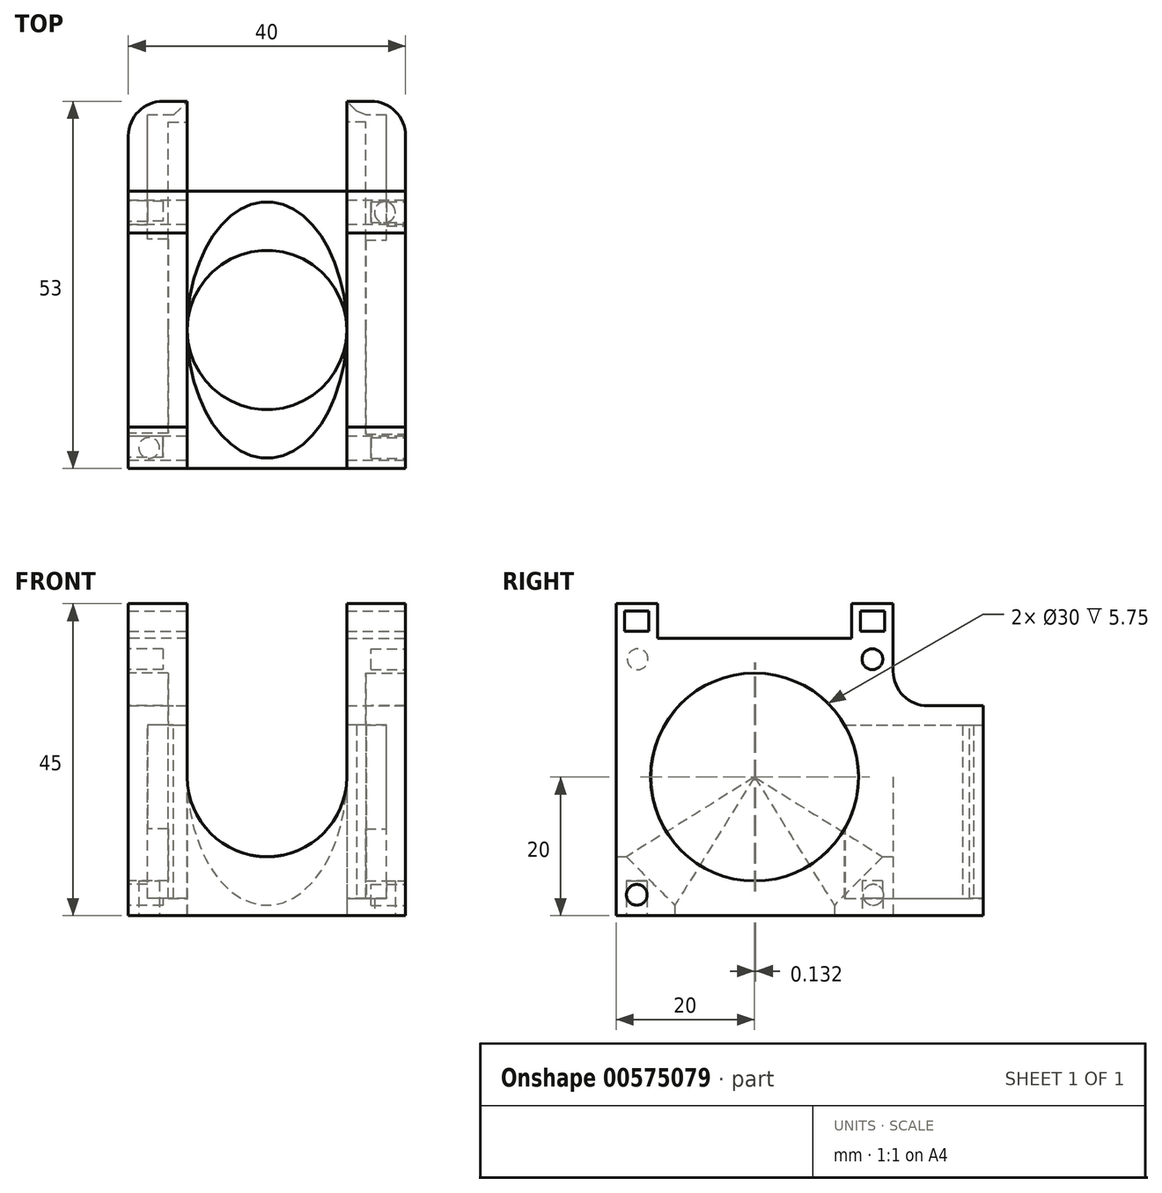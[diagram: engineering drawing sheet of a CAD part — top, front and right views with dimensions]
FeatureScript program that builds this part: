
annotation { "Feature Type Name" : "Feature", "Feature Type Description" : "" }
export const myFeature = defineFeature(function(context is Context, id is Id, definition is map)
    precondition{}
    {
        {
            var Q0;
            Q0=qCreatedBy(makeId("Front.planeOp"),FACE);
            var sketch = newSketch(context, id + "F0", { "sketchPlane" : qUnion([Q0])});
            skLineSegment(sketch, "E0", {"start": v(-20, 20) * mm, "end": v(-20, -20) * mm});
            skLineSegment(sketch, "E1", {"start": v(-20, -20) * mm, "end": v(20, -20) * mm});
            skLineSegment(sketch, "E2", {"start": v(20, -20) * mm, "end": v(20, 20) * mm});
            skLineSegment(sketch, "E3", {"start": v(20, 20) * mm, "end": v(11.5, 20) * mm});
            skLineSegment(sketch, "E4", {"start": v(11.5, 20) * mm, "end": v(11.5, 0) * mm});
            skLineSegment(sketch, "E5", {"start": v(-11.5, 0) * mm, "end": v(-11.5, 20) * mm});
            skLineSegment(sketch, "E6", {"start": v(-20, 20) * mm, "end": v(-11.5, 20) * mm});
            skLineSegment(sketch, "E7", {"start": v(0, 35.37) * mm, "end": v(0, -31.05) * mm, "construction": true});
            skLineSegment(sketch, "E8", {"start": v(-42.53, 0) * mm, "end": v(36.7, 0) * mm, "construction": true});
            skArc(sketch, "E9", {"start": v(-11.5, 0) * mm, "mid": v(0, -11.5) * mm, "end": v(11.5, 0) * mm});
            skSolve(sketch);
        }
        {
            var Q0;
            Q0 = qSketchRegion(id + "F0", true);
            extrude(context, id + "F1", {"entities" : qUnion([Q0]), "depth" : 40 * mm, "offsetDistance" : 25 * mm});
        }
        {
            var Q0;
            Q0=makeQuery(id+"F1.opExtrude","SWEPT_FACE",FACE,{"disambiguationData":[OSD([sQuery(id+"F0.wireOp",EDGE,"E1")])]});
            var sketch = newSketch(context, id + "F2", { "sketchPlane" : qUnion([Q0])});
            skLineSegment(sketch, "E10", {"start": v(-20, 40) * mm, "end": v(20, 0) * mm, "construction": true});
            skLineSegment(sketch, "E11", {"start": v(-20, 0) * mm, "end": v(20, 40) * mm, "construction": true});
            skCircle(sketch, "E12", {"center": v(0, 20) * mm, "radius": 11.5 * mm});
            skLineSegment(sketch, "E13", {"start": v(-17, 47.17) * mm, "end": v(-17, -3.7) * mm, "construction": true});
            skLineSegment(sketch, "E14", {"start": v(17, 46.33) * mm, "end": v(17, -4.22) * mm, "construction": true});
            skCircle(sketch, "E15", {"center": v(-17, 37) * mm, "radius": 1.5 * mm});
            skCircle(sketch, "E16", {"center": v(17, 3) * mm, "radius": 1.5 * mm});
            skSolve(sketch);
        }
        {
            var Q0;
            Q0=makeQuery(id+"F2.imprint","IMPRINT",FACE,{"disambiguationData":[TD([[makeQuery(id+"F2.imprint","IMPRINT",EDGE,{"derivedFrom":sQuery(id+"F2.wireOp",EDGE,"E12")}),1.0]])]});
            extrude(context, id + "F3", {"entities" : qUnion([Q0]), "operationType" : NewBodyOperationType.REMOVE, "oppositeDirection" : true, "depth" : 25 * mm, "offsetDistance" : 25 * mm});
        }
        {
            var Q0;
            Q0=makeQuery(id+"F2.imprint","IMPRINT",FACE,{"disambiguationData":[TD([[makeQuery(id+"F2.imprint","IMPRINT",EDGE,{"derivedFrom":sQuery(id+"F2.wireOp",EDGE,"E16")}),1.0]])]});
            var Q1;
            Q1=makeQuery(id+"F2.imprint","IMPRINT",FACE,{"disambiguationData":[TD([[makeQuery(id+"F2.imprint","IMPRINT",EDGE,{"derivedFrom":sQuery(id+"F2.wireOp",EDGE,"E15")}),1.0]])]});
            extrude(context, id + "F4", {"entities" : qUnion([Q0, Q1]), "operationType" : NewBodyOperationType.REMOVE, "oppositeDirection" : true, "depth" : 5 * mm, "offsetDistance" : 25 * mm});
        }
        {
            var Q0;
            Q0=makeQuery(id+"F1.opExtrude","SWEPT_FACE",FACE,{"disambiguationData":[OSD([sQuery(id+"F0.wireOp",EDGE,"E2")])]});
            var sketch = newSketch(context, id + "F5", { "sketchPlane" : qUnion([Q0])});
            skLineSegment(sketch, "E17", {"start": v(-40, -20) * mm, "end": v(0, 20) * mm, "construction": true});
            skCircle(sketch, "E18", {"center": v(-20, 0) * mm, "radius": 15 * mm});
            skLineSegment(sketch, "E19", {"start": v(7.6, -17) * mm, "end": v(-44.55, -17) * mm, "construction": true});
            skLineSegment(sketch, "E20", {"start": v(-46.22, 17) * mm, "end": v(4.75, 17) * mm, "construction": true});
            skCircle(sketch, "E21", {"center": v(-37, -17) * mm, "radius": 1.5 * mm});
            skCircle(sketch, "E22", {"center": v(-3, 17) * mm, "radius": 1.5 * mm});
            skSolve(sketch);
        }
        {
            var Q0;
            Q0=makeQuery(id+"F5.imprint","IMPRINT",FACE,{"disambiguationData":[TD([[makeQuery(id+"F5.imprint","IMPRINT",EDGE,{"derivedFrom":sQuery(id+"F5.wireOp",EDGE,"E18")}),1.0]])]});
            extrude(context, id + "F6", {"entities" : qUnion([Q0]), "operationType" : NewBodyOperationType.REMOVE, "oppositeDirection" : true, "depth" : 3 * mm, "offsetDistance" : 25 * mm});
        }
        {
            var Q0;
            Q0=makeQuery(id+"F5.imprint","IMPRINT",FACE,{"disambiguationData":[TD([[makeQuery(id+"F5.imprint","IMPRINT",EDGE,{"derivedFrom":sQuery(id+"F5.wireOp",EDGE,"E21")}),1.0]])]});
            var Q1;
            Q1=makeQuery(id+"F5.imprint","IMPRINT",FACE,{"disambiguationData":[TD([[makeQuery(id+"F5.imprint","IMPRINT",EDGE,{"derivedFrom":sQuery(id+"F5.wireOp",EDGE,"E22")}),1.0]])]});
            var Q2;
            Q2=sQuery(id+"F5.wireOp",EDGE,"E21");
            var Q3;
            Q3=sQuery(id+"F5.wireOp",EDGE,"E22");
            extrude(context, id + "F7", {"entities" : qUnion([Q0, Q1]), "operationType" : NewBodyOperationType.REMOVE, "surfaceEntities" : qUnion([Q2, Q3]), "oppositeDirection" : true, "depth" : 5 * mm, "offsetDistance" : 25 * mm});
        }
        {
            var Q0;
            Q0=makeQuery(id+"F1.opExtrude","CAP_FACE",FACE,{"disambiguationData":[OSD([sQuery(id+"F0.wireOp",EDGE,"E0"),sQuery(id+"F0.wireOp",EDGE,"E1"),sQuery(id+"F0.wireOp",EDGE,"E2"),sQuery(id+"F0.wireOp",EDGE,"E3"),sQuery(id+"F0.wireOp",EDGE,"E4"),sQuery(id+"F0.wireOp",EDGE,"E5"),sQuery(id+"F0.wireOp",EDGE,"E6"),sQuery(id+"F0.wireOp",EDGE,"E9")])],"isStart":true});
            var sketch = newSketch(context, id + "F8", { "sketchPlane" : qUnion([Q0])});
            skLineSegment(sketch, "E23", {"start": v(-20, -20) * mm, "end": v(-11.5, 20) * mm, "construction": true});
            skLineSegment(sketch, "E24.bottom", {"start": v(-14.25, 7.5) * mm, "end": v(-17.25, 7.5) * mm});
            skLineSegment(sketch, "E24.top", {"start": v(-14.25, -7.5) * mm, "end": v(-17.25, -7.5) * mm});
            skLineSegment(sketch, "E24.left", {"start": v(-14.25, 7.5) * mm, "end": v(-14.25, -7.5) * mm});
            skLineSegment(sketch, "E24.right", {"start": v(-17.25, 7.5) * mm, "end": v(-17.25, -7.5) * mm});
            skPoint(sketch, "E24.middle", {"position": v(-15.75, 0) * mm});
            skLineSegment(sketch, "E25", {"start": v(11.5, 20) * mm, "end": v(20, -20) * mm, "construction": true});
            skLineSegment(sketch, "E26.bottom", {"start": v(14.25, -7.5) * mm, "end": v(17.25, -7.5) * mm});
            skLineSegment(sketch, "E26.top", {"start": v(14.25, 7.5) * mm, "end": v(17.25, 7.5) * mm});
            skLineSegment(sketch, "E26.left", {"start": v(14.25, -7.5) * mm, "end": v(14.25, 7.5) * mm});
            skLineSegment(sketch, "E26.right", {"start": v(17.25, -7.5) * mm, "end": v(17.25, 7.5) * mm});
            skPoint(sketch, "E26.middle", {"position": v(15.75, 0) * mm});
            skSolve(sketch);
        }
        {
            var Q0;
            Q0 = qSketchRegion(id + "F8", true);
            extrude(context, id + "F9", {"entities" : qUnion([Q0]), "operationType" : NewBodyOperationType.REMOVE, "oppositeDirection" : true, "depth" : 20 * mm, "offsetDistance" : 25 * mm});
        }
        {
            var Q0;
            Q0=makeQuery(id+"F1.opExtrude","SWEPT_FACE",FACE,{"disambiguationData":[OSD([sQuery(id+"F0.wireOp",EDGE,"E0")])]});
            var sketch = newSketch(context, id + "F10", { "sketchPlane" : qUnion([Q0])});
            skLineSegment(sketch, "E27", {"start": v(-0.13, -20) * mm, "end": v(39.87, 20) * mm, "construction": true});
            skCircle(sketch, "E28", {"center": v(19.87, 0) * mm, "radius": 15 * mm});
            skLineSegment(sketch, "E29", {"start": v(47.47, -17) * mm, "end": v(-4.68, -17) * mm, "construction": true});
            skLineSegment(sketch, "E30", {"start": v(-6.36, 17) * mm, "end": v(44.62, 17) * mm, "construction": true});
            skCircle(sketch, "E31", {"center": v(2.87, -17) * mm, "radius": 1.5 * mm});
            skCircle(sketch, "E32", {"center": v(36.87, 17) * mm, "radius": 1.5 * mm});
            skSolve(sketch);
        }
        {
            var Q0;
            Q0=makeQuery(id+"F10.imprint","IMPRINT",FACE,{"disambiguationData":[TD([[makeQuery(id+"F10.imprint","IMPRINT",EDGE,{"derivedFrom":sQuery(id+"F10.wireOp",EDGE,"E28")}),1.0]])]});
            extrude(context, id + "F11", {"entities" : qUnion([Q0]), "operationType" : NewBodyOperationType.REMOVE, "oppositeDirection" : true, "depth" : 3 * mm, "offsetDistance" : 25 * mm});
        }
        {
            var Q0;
            Q0=makeQuery(id+"F10.imprint","IMPRINT",FACE,{"disambiguationData":[TD([[makeQuery(id+"F10.imprint","IMPRINT",EDGE,{"derivedFrom":sQuery(id+"F10.wireOp",EDGE,"E32")}),1.0]])]});
            var Q1;
            Q1=makeQuery(id+"F10.imprint","IMPRINT",FACE,{"disambiguationData":[TD([[makeQuery(id+"F10.imprint","IMPRINT",EDGE,{"derivedFrom":sQuery(id+"F10.wireOp",EDGE,"E31")}),1.0]])]});
            extrude(context, id + "F12", {"entities" : qUnion([Q0, Q1]), "operationType" : NewBodyOperationType.REMOVE, "oppositeDirection" : true, "depth" : 5 * mm, "offsetDistance" : 25 * mm});
        }
        {
            var Q0;
            Q0=makeQuery(id+"F1.opExtrude","CAP_FACE",FACE,{"disambiguationData":[OSD([sQuery(id+"F0.wireOp",EDGE,"E0"),sQuery(id+"F0.wireOp",EDGE,"E1"),sQuery(id+"F0.wireOp",EDGE,"E2"),sQuery(id+"F0.wireOp",EDGE,"E3"),sQuery(id+"F0.wireOp",EDGE,"E4"),sQuery(id+"F0.wireOp",EDGE,"E5"),sQuery(id+"F0.wireOp",EDGE,"E6"),sQuery(id+"F0.wireOp",EDGE,"E9")])],"isStart":true});
            extrude(context, id + "F13", {"entities" : qUnion([Q0]), "operationType" : NewBodyOperationType.ADD, "depth" : 13 * mm, "offsetDistance" : 25 * mm});
        }
        {
            var Q0;
            Q0=makeQuery(id+"F13.opExtrude","CAP_FACE",FACE,{"disambiguationData":[OSD([sQuery(id+"F0.wireOp",EDGE,"E0"),sQuery(id+"F0.wireOp",EDGE,"E1"),sQuery(id+"F0.wireOp",EDGE,"E2"),sQuery(id+"F0.wireOp",EDGE,"E3"),sQuery(id+"F0.wireOp",EDGE,"E4"),sQuery(id+"F0.wireOp",EDGE,"E5"),sQuery(id+"F0.wireOp",EDGE,"E6"),sQuery(id+"F0.wireOp",EDGE,"E9")])],"isStart":false});
            var sketch = newSketch(context, id + "F14", { "sketchPlane" : qUnion([Q0])});
            skLineSegment(sketch, "E33", {"start": v(20, -10.5) * mm, "end": v(-20, -10.5) * mm});
            skLineSegment(sketch, "E34", {"start": v(11.5, 20) * mm, "end": v(11.5, -10.5) * mm});
            skLineSegment(sketch, "E35", {"start": v(-11.5, 20) * mm, "end": v(-11.5, -10.5) * mm});
            skLineSegment(sketch, "E36", {"start": v(20, 10.28) * mm, "end": v(-20, 10.28) * mm});
            skSolve(sketch);
        }
        {
            var Q0;
            {var subQ0=makeQuery(id+"F13.opExtrude","CAP_EDGE",EDGE,{"disambiguationData":[OSD([sQuery(id+"F0.wireOp",EDGE,"E1")])],"isStart":false});Q0=makeQuery(id+"F14.imprint","IMPRINT",FACE,{"disambiguationData":[TD([[makeQuery(id+"F14.imprint","IMPRINT",EDGE,{"derivedFrom":subQ0}),-1.0]])]});}
            var Q1;
            {var subQ0=sQuery(id+"F14.wireOp",EDGE,"E34");var subQ1=sQuery(id+"F14.wireOp",EDGE,"E33");var subQ2=makeQuery(id+"F14.imprint","INTERSECT",VERTEX,{"derivedFrom":[subQ1,subQ0]});Q1=makeQuery(id+"F14.imprint","IMPRINT",FACE,{"disambiguationData":[TD([[makeQuery(id+"F14.imprint","IMPRINT",EDGE,{"disambiguationData":[TD([[subQ2,-1.0]])],"derivedFrom":subQ1}),-1.0]])]});}
            var Q2;
            {var subQ0=sQuery(id+"F14.wireOp",EDGE,"E35");var subQ1=sQuery(id+"F14.wireOp",EDGE,"E33");var subQ2=makeQuery(id+"F14.imprint","INTERSECT",VERTEX,{"derivedFrom":[subQ1,subQ0]});Q2=makeQuery(id+"F14.imprint","IMPRINT",FACE,{"disambiguationData":[TD([[makeQuery(id+"F14.imprint","IMPRINT",EDGE,{"disambiguationData":[TD([[subQ2,1.0]])],"derivedFrom":subQ1}),-1.0]])]});}
            var Q3;
            {var subQ1=makeQuery(id+"F13.opExtrude","CAP_EDGE",EDGE,{"disambiguationData":[OSD([sQuery(id+"F0.wireOp",EDGE,"E6")])],"isStart":false});Q3=makeQuery(id+"F14.imprint","IMPRINT",FACE,{"disambiguationData":[TD([[makeQuery(id+"F14.imprint","IMPRINT",EDGE,{"derivedFrom":subQ1}),1.0]])]});}
            var Q4;
            {var subQ1=makeQuery(id+"F13.opExtrude","CAP_EDGE",EDGE,{"disambiguationData":[OSD([sQuery(id+"F0.wireOp",EDGE,"E3")])],"isStart":false});Q4=makeQuery(id+"F14.imprint","IMPRINT",FACE,{"disambiguationData":[TD([[makeQuery(id+"F14.imprint","IMPRINT",EDGE,{"derivedFrom":subQ1}),-1.0]])]});}
            extrude(context, id + "F15", {"entities" : qUnion([Q0, Q1, Q2, Q3, Q4]), "operationType" : NewBodyOperationType.REMOVE, "oppositeDirection" : true, "depth" : 13 * mm, "offsetDistance" : 25 * mm});
        }
        {
            var Q0;
            Q0=makeQuery(id+"F14.imprint","IMPRINT",FACE,{"disambiguationData":[TD([[makeQuery(id+"F14.imprint","IMPRINT",EDGE,{"derivedFrom":makeQuery(id+"F13.opExtrude","CAP_EDGE",EDGE,{"disambiguationData":[OSD([sQuery(id+"F8.wireOp",EDGE,"E26.bottom")])],"isStart":false})}),-1.0]])]});
            var sketch = newSketch(context, id + "F16", { "sketchPlane" : qUnion([Q0])});
            skLineSegment(sketch, "E37.0", {"start": v(11.5, 20) * mm, "end": v(11.5, -10.5) * mm});
            skLineSegment(sketch, "E38.0", {"start": v(14.25, -7.5) * mm, "end": v(14.25, 7.5) * mm});
            skLineSegment(sketch, "E39.bottom", {"start": v(14.25, -7.5) * mm, "end": v(11.5, -7.5) * mm});
            skLineSegment(sketch, "E39.top", {"start": v(14.25, 7.5) * mm, "end": v(11.5, 7.5) * mm});
            skLineSegment(sketch, "E39.right", {"start": v(11.5, -7.5) * mm, "end": v(11.5, 7.5) * mm});
            skLineSegment(sketch, "E40.0", {"start": v(-14.25, 7.5) * mm, "end": v(-14.25, -7.5) * mm});
            skLineSegment(sketch, "E41.0", {"start": v(-11.5, 20) * mm, "end": v(-11.5, -10.5) * mm});
            skLineSegment(sketch, "E42.bottom", {"start": v(-14.25, -7.5) * mm, "end": v(-11.5, -7.5) * mm});
            skLineSegment(sketch, "E42.top", {"start": v(-14.25, 7.5) * mm, "end": v(-11.5, 7.5) * mm});
            skLineSegment(sketch, "E42.left", {"start": v(-14.25, -7.5) * mm, "end": v(-14.25, 7.5) * mm});
            skLineSegment(sketch, "E42.right", {"start": v(-11.5, -7.5) * mm, "end": v(-11.5, 7.5) * mm});
            skSolve(sketch);
        }
        {
            var Q0;
            Q0 = qSketchRegion(id + "F16", true);
            extrude(context, id + "F17", {"entities" : qUnion([Q0]), "operationType" : NewBodyOperationType.REMOVE, "oppositeDirection" : true, "depth" : 3 * mm, "offsetDistance" : 25 * mm});
        }
        {
            var Q0;
            {var subQ0=sQuery(id+"F14.wireOp",EDGE,"E36");Q0=makeQuery(id+"F15.boolean.opBoolean","COPY",FACE,{"derivedFrom":makeQuery(id+"F15.opExtrude","SWEPT_FACE",FACE,{"disambiguationData":[OSD([subQ0]),TDD([makeQuery(id+"F14.imprint","IMPRINT",EDGE,{"disambiguationData":[TD([[makeQuery(id+"F14.imprint","INTERSECT",VERTEX,{"derivedFrom":[makeQuery(id+"F13.opExtrude","CAP_EDGE",EDGE,{"disambiguationData":[OSD([sQuery(id+"F0.wireOp",EDGE,"E0")])],"isStart":false}),subQ0]}),-1.0]])],"derivedFrom":subQ0})])]})});}
            var sketch = newSketch(context, id + "F18", { "sketchPlane" : qUnion([Q0])});
            skLineSegment(sketch, "E43", {"start": v(-20, 11) * mm, "end": v(-11.5, 11) * mm});
            skSolve(sketch);
        }
        {
            var Q0;
            {var subQ0=sQuery(id+"F18.wireOp",EDGE,"E43");Q0=makeQuery(id+"F18.imprint","IMPRINT",FACE,{"disambiguationData":[TD([[makeQuery(id+"F18.imprint","IMPRINT",EDGE,{"derivedFrom":subQ0}),1.0]])]});}
            extrude(context, id + "F19", {"entities" : qUnion([Q0]), "operationType" : NewBodyOperationType.ADD, "oppositeDirection" : true, "depth" : 18 * mm, "offsetDistance" : 25 * mm});
        }
        {
            var Q0;
            {var subQ0=sQuery(id+"F0.wireOp",EDGE,"E4");var subQ1=sQuery(id+"F0.wireOp",EDGE,"E2");var subQ10=sQuery(id+"F0.wireOp",EDGE,"E9");Q0=makeQuery(id+"F15.boolean.opBoolean","SPLIT",FACE,{"disambiguationData":[TD([makeQuery(id+"F1.opExtrude","SWEPT_FACE",FACE,{"disambiguationData":[OSD([subQ1])]})])],"derivedFrom":makeQuery(id+"F13.opExtrude","CAP_FACE",FACE,{"disambiguationData":[OSD([sQuery(id+"F0.wireOp",EDGE,"E0"),sQuery(id+"F0.wireOp",EDGE,"E1"),subQ1,sQuery(id+"F0.wireOp",EDGE,"E3"),subQ0,sQuery(id+"F0.wireOp",EDGE,"E5"),sQuery(id+"F0.wireOp",EDGE,"E6"),subQ10])],"isStart":false})});}
            var sketch = newSketch(context, id + "F20", { "sketchPlane" : qUnion([Q0])});
            skLineSegment(sketch, "E44.bottom", {"start": v(-20, 10.28) * mm, "end": v(-11.5, 10.28) * mm});
            skLineSegment(sketch, "E44.top", {"start": v(-20, -10.5) * mm, "end": v(-11.5, -10.5) * mm});
            skLineSegment(sketch, "E44.left", {"start": v(-20, 10.28) * mm, "end": v(-20, -10.5) * mm});
            skLineSegment(sketch, "E44.right", {"start": v(-11.5, 10.28) * mm, "end": v(-11.5, -10.5) * mm});
            skSolve(sketch);
        }
        {
            var Q0;
            Q0 = qSketchRegion(id + "F20", true);
            extrude(context, id + "F21", {"entities" : qUnion([Q0]), "operationType" : NewBodyOperationType.ADD, "oppositeDirection" : true, "depth" : 2 * mm, "offsetDistance" : 25 * mm});
        }
        {
            var Q0;
            Q0=makeQuery(id+"F19.opExtrude","SWEPT_EDGE",EDGE,{"disambiguationData":[OSD([sQuery(id+"F14.wireOp",EDGE,"E34"),sQuery(id+"F14.wireOp",EDGE,"E36"),sQuery(id+"F18.wireOp",EDGE,"E43")])]});
            var Q1;
            Q1=makeQuery(id+"F17.boolean.opBoolean","COPY",EDGE,{"derivedFrom":makeQuery(id+"F17.opExtrude","CAP_EDGE",EDGE,{"disambiguationData":[OSD([sQuery(id+"F16.wireOp",EDGE,"E38.0")])],"isStart":false})});
            var Q2;
            Q2=makeQuery(id+"F17.boolean.opBoolean","COPY",EDGE,{"derivedFrom":makeQuery(id+"F17.opExtrude","CAP_EDGE",EDGE,{"disambiguationData":[OSD([sQuery(id+"F16.wireOp",EDGE,"E42.left")])],"isStart":false})});
            var Q3;
            Q3=makeQuery(id+"F21.opExtrude","CAP_EDGE",EDGE,{"disambiguationData":[OSD([sQuery(id+"F20.wireOp",EDGE,"E44.right")])],"isStart":false});
            chamfer(context, id + "F22", {"entities" : qUnion([Q0, Q1, Q2, Q3]), "width" : 2 * mm, "tangentPropagation" : true});
        }
        {
            var Q0;
            {var subQ0=sQuery(id+"F18.wireOp",EDGE,"E43");Q0=makeQuery(id+"F22.opChamfer","BLEND_EDGE",EDGE,{"blendedFrom":[makeQuery(id+"F19.opExtrude","SWEPT_EDGE",EDGE,{"disambiguationData":[OSD([sQuery(id+"F14.wireOp",EDGE,"E34"),sQuery(id+"F14.wireOp",EDGE,"E36"),subQ0])]}),makeQuery(id+"FBn1wkCs05xnqRL_1.opFillet","BLEND_FACE",FACE,{"disambiguationData":[OSD([sQuery(id+"F8.wireOp",EDGE,"E26.right"),subQ0])]})],"blendedInto":[makeQuery(id+"FBn1wkCs05xnqRL_1.opFillet","BLEND_FACE",FACE,{"disambiguationData":[OSD([sQuery(id+"F8.wireOp",EDGE,"E26.right"),subQ0])]})]});}
            var Q1;
            {var subQ0=sQuery(id+"F20.wireOp",EDGE,"E44.right");Q1=makeQuery(id+"F22.opChamfer","BLEND_EDGE",EDGE,{"blendedFrom":[makeQuery(id+"F21.opExtrude","CAP_EDGE",EDGE,{"disambiguationData":[OSD([subQ0])],"isStart":false}),makeQuery(id+"F21.opExtrude","CAP_FACE",FACE,{"disambiguationData":[OSD([sQuery(id+"F20.wireOp",EDGE,"E44.bottom"),sQuery(id+"F20.wireOp",EDGE,"E44.top"),sQuery(id+"F20.wireOp",EDGE,"E44.left"),subQ0])],"isStart":false})],"blendedInto":[makeQuery(id+"F21.opExtrude","CAP_FACE",FACE,{"disambiguationData":[OSD([sQuery(id+"F20.wireOp",EDGE,"E44.bottom"),sQuery(id+"F20.wireOp",EDGE,"E44.top"),sQuery(id+"F20.wireOp",EDGE,"E44.left"),subQ0])],"isStart":false})]});}
            chamfer(context, id + "F23", {"entities" : qUnion([Q0, Q1]), "width" : 2 * mm, "tangentPropagation" : true});
        }
        {
            var Q0;
            Q0=makeQuery(id+"F3.boolean.opBoolean","COPY",EDGE,{"derivedFrom":makeQuery(id+"F3.opExtrude","CAP_EDGE",EDGE,{"disambiguationData":[OSD([sQuery(id+"F2.wireOp",EDGE,"E12")])],"isStart":true})});
            var Q1;
            Q1=makeQuery(id+"F3.boolean.opBoolean","INTERSECT",EDGE,{"disambiguationData":[OD(1.0)],"derivedFrom":[makeQuery(id+"F1.opExtrude","SWEPT_FACE",FACE,{"disambiguationData":[OSD([sQuery(id+"F0.wireOp",EDGE,"E9")])]}),makeQuery(id+"F3.opExtrude","SWEPT_FACE",FACE,{"disambiguationData":[OSD([sQuery(id+"F2.wireOp",EDGE,"E12")])]})]});
            var Q2;
            Q2=makeQuery(id+"F3.boolean.opBoolean","INTERSECT",EDGE,{"disambiguationData":[OD(0.0)],"derivedFrom":[makeQuery(id+"F1.opExtrude","SWEPT_FACE",FACE,{"disambiguationData":[OSD([sQuery(id+"F0.wireOp",EDGE,"E9")])]}),makeQuery(id+"F3.opExtrude","SWEPT_FACE",FACE,{"disambiguationData":[OSD([sQuery(id+"F2.wireOp",EDGE,"E12")])]})]});
            chamfer(context, id + "F24", {"entities" : qUnion([Q0, Q1, Q2]), "width" : 7 * mm, "tangentPropagation" : true});
        }
        {
            var Q0;
            Q0=makeQuery(id+"F11.boolean.opBoolean","COPY",FACE,{"derivedFrom":makeQuery(id+"F11.opExtrude","CAP_FACE",FACE,{"disambiguationData":[OSD([sQuery(id+"F10.wireOp",EDGE,"E28")])],"isStart":false})});
            extrude(context, id + "F25", {"entities" : qUnion([Q0]), "operationType" : NewBodyOperationType.REMOVE, "oppositeDirection" : true, "depth" : 2.75 * mm, "offsetDistance" : 25 * mm});
        }
        {
            var Q0;
            Q0=makeQuery(id+"F6.boolean.opBoolean","COPY",FACE,{"derivedFrom":makeQuery(id+"F6.opExtrude","CAP_FACE",FACE,{"disambiguationData":[OSD([sQuery(id+"F5.wireOp",EDGE,"E18")])],"isStart":false})});
            extrude(context, id + "F26", {"entities" : qUnion([Q0]), "operationType" : NewBodyOperationType.REMOVE, "oppositeDirection" : true, "depth" : 2.75 * mm, "offsetDistance" : 25 * mm});
        }
        {
            var Q0;
            {var subQ0=sQuery(id+"F0.wireOp",EDGE,"E3");Q0=makeQuery(id+"F13.boolean.opBoolean","MERGE",FACE,{"derivedFrom":[makeQuery(id+"F1.opExtrude","SWEPT_FACE",FACE,{"disambiguationData":[OSD([subQ0])]}),makeQuery(id+"F13.opExtrude","SWEPT_FACE",FACE,{"disambiguationData":[OSD([subQ0])]})]});}
            var sketch = newSketch(context, id + "F27", { "sketchPlane" : qUnion([Q0])});
            skLineSegment(sketch, "E45.bottom", {"start": v(11.5, -40) * mm, "end": v(20, -40) * mm});
            skLineSegment(sketch, "E45.top", {"start": v(11.5, -34) * mm, "end": v(20, -34) * mm});
            skLineSegment(sketch, "E45.left", {"start": v(11.5, -40) * mm, "end": v(11.5, -34) * mm});
            skLineSegment(sketch, "E45.right", {"start": v(20, -40) * mm, "end": v(20, -34) * mm});
            skLineSegment(sketch, "E46.bottom", {"start": v(11.5, 0) * mm, "end": v(20, 0) * mm});
            skLineSegment(sketch, "E46.top", {"start": v(11.5, -6) * mm, "end": v(20, -6) * mm});
            skLineSegment(sketch, "E46.left", {"start": v(11.5, 0) * mm, "end": v(11.5, -6) * mm});
            skLineSegment(sketch, "E46.right", {"start": v(20, 0) * mm, "end": v(20, -6) * mm});
            skSolve(sketch);
        }
        {
            var Q0;
            Q0 = qSketchRegion(id + "F27", true);
            extrude(context, id + "F28", {"entities" : qUnion([Q0]), "operationType" : NewBodyOperationType.ADD, "depth" : 5 * mm, "offsetDistance" : 25 * mm});
        }
        {
            var Q0;
            {var subQ0=sQuery(id+"F0.wireOp",EDGE,"E6");Q0=makeQuery(id+"F13.boolean.opBoolean","MERGE",FACE,{"derivedFrom":[makeQuery(id+"F1.opExtrude","SWEPT_FACE",FACE,{"disambiguationData":[OSD([subQ0])]}),makeQuery(id+"F13.opExtrude","SWEPT_FACE",FACE,{"disambiguationData":[OSD([subQ0])]})]});}
            var sketch = newSketch(context, id + "F29", { "sketchPlane" : qUnion([Q0])});
            skLineSegment(sketch, "E47.bottom", {"start": v(-11.5, -40) * mm, "end": v(-20, -40) * mm});
            skLineSegment(sketch, "E47.top", {"start": v(-11.5, -34) * mm, "end": v(-20, -34) * mm});
            skLineSegment(sketch, "E47.left", {"start": v(-11.5, -40) * mm, "end": v(-11.5, -34) * mm});
            skLineSegment(sketch, "E47.right", {"start": v(-20, -40) * mm, "end": v(-20, -34) * mm});
            skLineSegment(sketch, "E48.bottom", {"start": v(-11.5, 0) * mm, "end": v(-20, 0) * mm});
            skLineSegment(sketch, "E48.top", {"start": v(-11.5, -6) * mm, "end": v(-20, -6) * mm});
            skLineSegment(sketch, "E48.left", {"start": v(-11.5, 0) * mm, "end": v(-11.5, -6) * mm});
            skLineSegment(sketch, "E48.right", {"start": v(-20, 0) * mm, "end": v(-20, -6) * mm});
            skSolve(sketch);
        }
        {
            var Q0;
            Q0 = qSketchRegion(id + "F29", true);
            extrude(context, id + "F30", {"entities" : qUnion([Q0]), "operationType" : NewBodyOperationType.ADD, "depth" : 5 * mm, "offsetDistance" : 25 * mm});
        }
        {
            var Q0;
            {var subQ0=sQuery(id+"F0.wireOp",EDGE,"E2");Q0=makeQuery(id+"F28.boolean.opBoolean","MERGE",FACE,{"derivedFrom":[makeQuery(id+"F13.boolean.opBoolean","MERGE",FACE,{"derivedFrom":[makeQuery(id+"F1.opExtrude","SWEPT_FACE",FACE,{"disambiguationData":[OSD([subQ0])]}),makeQuery(id+"F13.opExtrude","SWEPT_FACE",FACE,{"disambiguationData":[OSD([subQ0])]})]}),makeQuery(id+"F28.opExtrude","SWEPT_FACE",FACE,{"disambiguationData":[OSD([sQuery(id+"F27.wireOp",EDGE,"E45.right")])]}),makeQuery(id+"F28.opExtrude","SWEPT_FACE",FACE,{"disambiguationData":[OSD([sQuery(id+"F27.wireOp",EDGE,"E46.right")])]})]});}
            var sketch = newSketch(context, id + "F31", { "sketchPlane" : qUnion([Q0])});
            skLineSegment(sketch, "E49", {"start": v(-40, 25) * mm, "end": v(-34, 20) * mm, "construction": true});
            skLineSegment(sketch, "E50", {"start": v(0, 25) * mm, "end": v(-6, 20) * mm, "construction": true});
            skLineSegment(sketch, "E51.bottom", {"start": v(-35.25, 21.04) * mm, "end": v(-38.75, 21.04) * mm});
            skLineSegment(sketch, "E51.top", {"start": v(-35.25, 23.96) * mm, "end": v(-38.75, 23.96) * mm});
            skLineSegment(sketch, "E51.left", {"start": v(-35.25, 21.04) * mm, "end": v(-35.25, 23.96) * mm});
            skLineSegment(sketch, "E51.right", {"start": v(-38.75, 21.04) * mm, "end": v(-38.75, 23.96) * mm});
            skPoint(sketch, "E51.middle", {"position": v(-37, 22.5) * mm});
            skLineSegment(sketch, "E52.bottom", {"start": v(-4.75, 21.04) * mm, "end": v(-1.25, 21.04) * mm});
            skLineSegment(sketch, "E52.top", {"start": v(-4.75, 23.96) * mm, "end": v(-1.25, 23.96) * mm});
            skLineSegment(sketch, "E52.left", {"start": v(-4.75, 21.04) * mm, "end": v(-4.75, 23.96) * mm});
            skLineSegment(sketch, "E52.right", {"start": v(-1.25, 21.04) * mm, "end": v(-1.25, 23.96) * mm});
            skPoint(sketch, "E52.middle", {"position": v(-3, 22.5) * mm});
            skSolve(sketch);
        }
        {
            var Q0;
            Q0 = qSketchRegion(id + "F31", true);
            extrude(context, id + "F32", {"entities" : qUnion([Q0]), "operationType" : NewBodyOperationType.REMOVE, "oppositeDirection" : true, "depth" : 50 * mm, "offsetDistance" : 25 * mm});
        }
        {
            var Q0;
            {var subQ0=sQuery(id+"F14.wireOp",EDGE,"E33");Q0=makeQuery(id+"F15.boolean.opBoolean","COPY",FACE,{"derivedFrom":makeQuery(id+"F15.opExtrude","SWEPT_FACE",FACE,{"disambiguationData":[OSD([subQ0]),TDD([makeQuery(id+"F14.imprint","IMPRINT",EDGE,{"disambiguationData":[TD([[makeQuery(id+"F14.imprint","INTERSECT",VERTEX,{"derivedFrom":[makeQuery(id+"F13.opExtrude","CAP_EDGE",EDGE,{"disambiguationData":[OSD([sQuery(id+"F0.wireOp",EDGE,"E2")])],"isStart":false}),subQ0]}),1.0]])],"derivedFrom":subQ0})])]})});}
            var Q1;
            {var subQ0=sQuery(id+"F14.wireOp",EDGE,"E33");Q1=makeQuery(id+"F15.boolean.opBoolean","COPY",FACE,{"derivedFrom":makeQuery(id+"F15.opExtrude","SWEPT_FACE",FACE,{"disambiguationData":[OSD([subQ0]),TDD([makeQuery(id+"F14.imprint","IMPRINT",EDGE,{"disambiguationData":[TD([[makeQuery(id+"F14.imprint","INTERSECT",VERTEX,{"derivedFrom":[makeQuery(id+"F13.opExtrude","CAP_EDGE",EDGE,{"disambiguationData":[OSD([sQuery(id+"F0.wireOp",EDGE,"E0")])],"isStart":false}),subQ0]}),-1.0]])],"derivedFrom":subQ0})])]})});}
            extrude(context, id + "F33", {"entities" : qUnion([Q0, Q1]), "operationType" : NewBodyOperationType.ADD, "depth" : 9.5 * mm, "offsetDistance" : 25 * mm});
        }
        {
            var Q0;
            {var subQ0=sQuery(id+"F8.wireOp",EDGE,"E24.top");Q0=makeQuery(id+"F17.boolean.opBoolean","MERGE",FACE,{"derivedFrom":[makeQuery(id+"F13.boolean.opBoolean","MERGE",FACE,{"derivedFrom":[makeQuery(id+"F9.boolean.opBoolean","COPY",FACE,{"derivedFrom":makeQuery(id+"F9.opExtrude","SWEPT_FACE",FACE,{"disambiguationData":[OSD([subQ0])]})}),makeQuery(id+"F13.opExtrude","SWEPT_FACE",FACE,{"disambiguationData":[OSD([subQ0])]})]}),makeQuery(id+"F17.opExtrude","SWEPT_FACE",FACE,{"disambiguationData":[OSD([sQuery(id+"F16.wireOp",EDGE,"E42.bottom")])]})]});}
            extrude(context, id + "F34", {"entities" : qUnion([Q0]), "operationType" : NewBodyOperationType.REMOVE, "oppositeDirection" : true, "depth" : 10 * mm, "offsetDistance" : 25 * mm});
        }
        {
            var Q0;
            {var subQ0=sQuery(id+"F8.wireOp",EDGE,"E26.bottom");Q0=makeQuery(id+"F17.boolean.opBoolean","MERGE",FACE,{"derivedFrom":[makeQuery(id+"F13.boolean.opBoolean","MERGE",FACE,{"derivedFrom":[makeQuery(id+"F9.boolean.opBoolean","COPY",FACE,{"derivedFrom":makeQuery(id+"F9.opExtrude","SWEPT_FACE",FACE,{"disambiguationData":[OSD([subQ0])]})}),makeQuery(id+"F13.opExtrude","SWEPT_FACE",FACE,{"disambiguationData":[OSD([subQ0])]})]}),makeQuery(id+"F17.opExtrude","SWEPT_FACE",FACE,{"disambiguationData":[OSD([sQuery(id+"F16.wireOp",EDGE,"E39.bottom")])]})]});}
            extrude(context, id + "F35", {"entities" : qUnion([Q0]), "operationType" : NewBodyOperationType.REMOVE, "oppositeDirection" : true, "depth" : 10 * mm, "offsetDistance" : 25 * mm});
        }
        {
            var Q0;
            {var subQ0=sQuery(id+"F14.wireOp",EDGE,"E33");var subQ1=sQuery(id+"F0.wireOp",EDGE,"E2");Q0=makeQuery(id+"F33.boolean.opBoolean","MERGE",EDGE,{"derivedFrom":[makeQuery(id+"F13.opExtrude","CAP_EDGE",EDGE,{"disambiguationData":[OSD([subQ1])],"isStart":false}),makeQuery(id+"F33.opExtrude","SWEPT_EDGE",EDGE,{"disambiguationData":[OSD([subQ1,subQ0]),TDD([makeQuery(id+"F15.boolean.opBoolean","COPY",VERTEX,{"derivedFrom":makeQuery(id+"F15.opExtrude","CAP_VERTEX",VERTEX,{"disambiguationData":[OSD([subQ1,subQ0])],"isStart":true})})])]})]});}
            var Q1;
            {var subQ0=sQuery(id+"F14.wireOp",EDGE,"E36");Q1=makeQuery(id+"F15.boolean.opBoolean","COPY",EDGE,{"derivedFrom":makeQuery(id+"F15.opExtrude","CAP_EDGE",EDGE,{"disambiguationData":[OSD([subQ0]),TDD([makeQuery(id+"F14.imprint","IMPRINT",EDGE,{"disambiguationData":[TD([[makeQuery(id+"F14.imprint","INTERSECT",VERTEX,{"derivedFrom":[makeQuery(id+"F13.opExtrude","CAP_EDGE",EDGE,{"disambiguationData":[OSD([sQuery(id+"F0.wireOp",EDGE,"E2")])],"isStart":false}),subQ0]}),1.0]])],"derivedFrom":subQ0})])],"isStart":false})});}
            var Q2;
            {var subQ0=sQuery(id+"F14.wireOp",EDGE,"E33");var subQ1=sQuery(id+"F0.wireOp",EDGE,"E0");Q2=makeQuery(id+"F33.boolean.opBoolean","MERGE",EDGE,{"derivedFrom":[makeQuery(id+"F13.opExtrude","CAP_EDGE",EDGE,{"disambiguationData":[OSD([subQ1])],"isStart":false}),makeQuery(id+"F33.opExtrude","SWEPT_EDGE",EDGE,{"disambiguationData":[OSD([subQ1,subQ0]),TDD([makeQuery(id+"F15.boolean.opBoolean","COPY",VERTEX,{"derivedFrom":makeQuery(id+"F15.opExtrude","CAP_VERTEX",VERTEX,{"disambiguationData":[OSD([subQ1,subQ0])],"isStart":true})})])]})]});}
            var Q3;
            {var subQ0=sQuery(id+"F14.wireOp",EDGE,"E36");Q3=makeQuery(id+"F15.boolean.opBoolean","COPY",EDGE,{"derivedFrom":makeQuery(id+"F15.opExtrude","CAP_EDGE",EDGE,{"disambiguationData":[OSD([subQ0]),TDD([makeQuery(id+"F14.imprint","IMPRINT",EDGE,{"disambiguationData":[TD([[makeQuery(id+"F14.imprint","INTERSECT",VERTEX,{"derivedFrom":[makeQuery(id+"F13.opExtrude","CAP_EDGE",EDGE,{"disambiguationData":[OSD([sQuery(id+"F0.wireOp",EDGE,"E0")])],"isStart":false}),subQ0]}),-1.0]])],"derivedFrom":subQ0})])],"isStart":false})});}
            var Q4;
            Q4=makeQuery(id+"F30.opExtrude","CAP_EDGE",EDGE,{"disambiguationData":[OSD([sQuery(id+"F29.wireOp",EDGE,"E48.top")])],"isStart":true});
            var Q5;
            Q5=makeQuery(id+"F28.opExtrude","CAP_EDGE",EDGE,{"disambiguationData":[OSD([sQuery(id+"F27.wireOp",EDGE,"E46.top")])],"isStart":true});
            var Q6;
            Q6=makeQuery(id+"F28.opExtrude","CAP_EDGE",EDGE,{"disambiguationData":[OSD([sQuery(id+"F27.wireOp",EDGE,"E45.top")])],"isStart":true});
            var Q7;
            Q7=makeQuery(id+"F30.opExtrude","CAP_EDGE",EDGE,{"disambiguationData":[OSD([sQuery(id+"F29.wireOp",EDGE,"E47.top")])],"isStart":true});
            fillet(context, id + "F36", {"entities" : qUnion([Q0, Q1, Q2, Q3, Q4, Q5, Q6, Q7]), "radius" : 5 * mm, "tangentPropagation" : true, "allowEdgeOverflow" : false});
        }
    });
